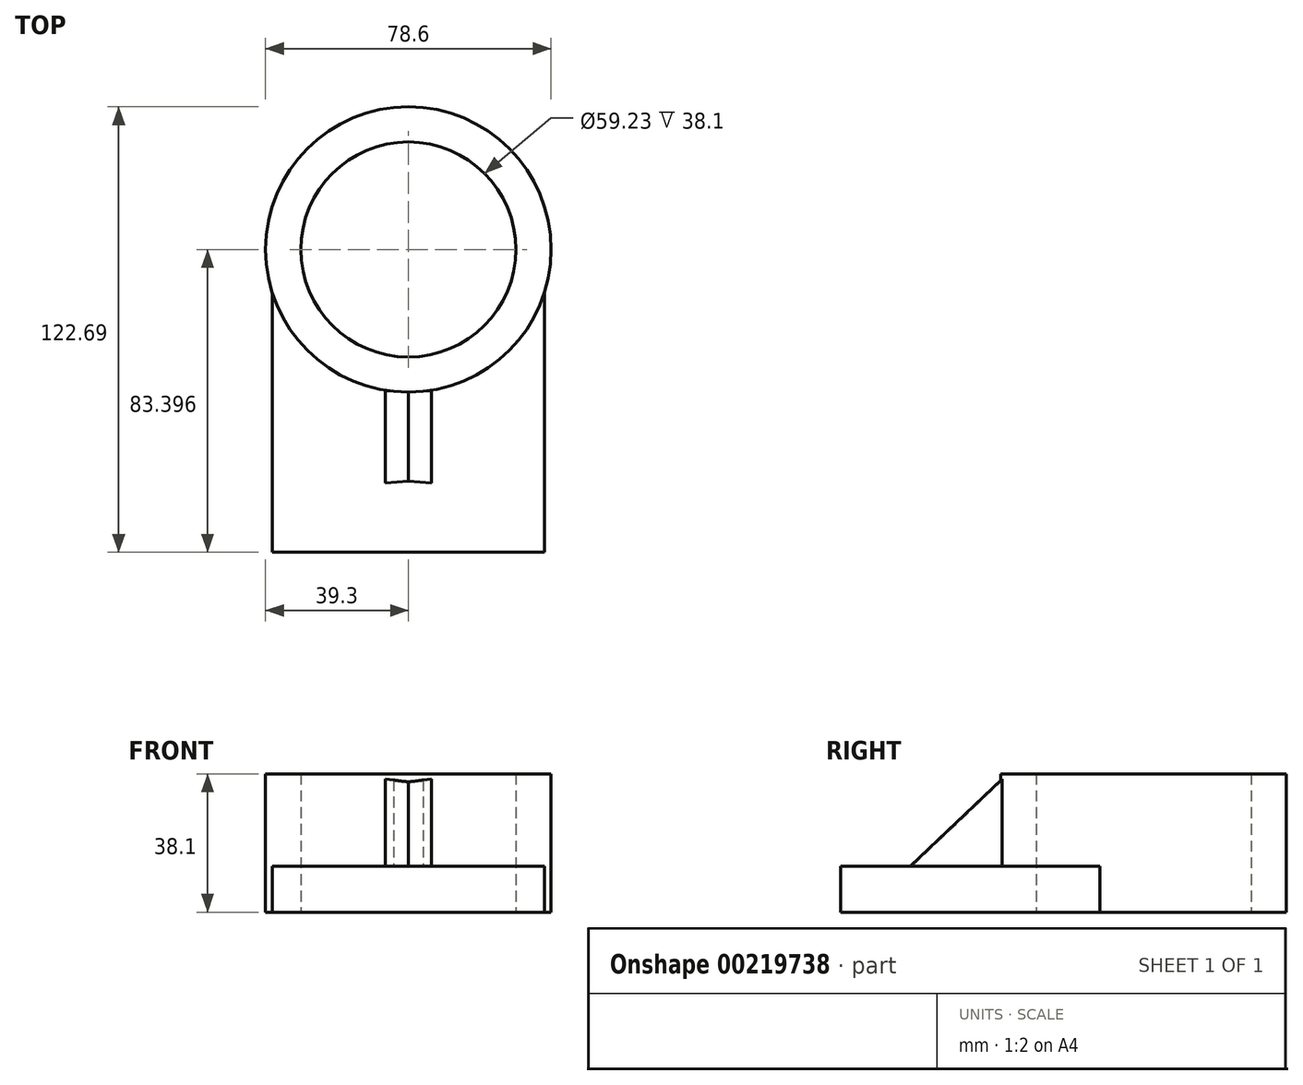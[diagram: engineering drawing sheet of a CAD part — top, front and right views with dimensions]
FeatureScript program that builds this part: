
annotation { "Feature Type Name" : "Feature", "Feature Type Description" : "" }
export const myFeature = defineFeature(function(context is Context, id is Id, definition is map)
    precondition{}
    {
        {
            var Q0;
            Q0=qCreatedBy(makeId("Top.planeOp"),FACE);
            var sketch = newSketch(context, id + "F0", { "sketchPlane" : qUnion([Q0])});
            skLineSegment(sketch, "E0.bottom", {"start": v(37.4, -35.68) * mm, "end": v(-37.4, -35.68) * mm});
            skLineSegment(sketch, "E0.top", {"start": v(37.4, 35.68) * mm, "end": v(-37.4, 35.68) * mm});
            skLineSegment(sketch, "E0.left", {"start": v(37.4, -35.68) * mm, "end": v(37.4, 35.68) * mm});
            skLineSegment(sketch, "E0.right", {"start": v(-37.4, -35.68) * mm, "end": v(-37.4, 35.68) * mm});
            skPoint(sketch, "E0.middle", {"position": v(0, 0) * mm});
            skSolve(sketch);
        }
        {
            var Q0;
            Q0=makeQuery(id+"F0.imprint","IMPRINT",FACE,{"disambiguationData":[TD([[makeQuery(id+"F0.imprint","IMPRINT",EDGE,{"derivedFrom":sQuery(id+"F0.wireOp",EDGE,"E0.bottom")}),-1.0]])]});
            extrude(context, id + "F1", {"entities" : qUnion([Q0]), "depth" : 12.7 * mm});
        }
        {
            var Q0;
            Q0=makeQuery(id+"F1.opExtrude","CAP_FACE",FACE,{"disambiguationData":[OSD([sQuery(id+"F0.wireOp",EDGE,"E0.bottom"),sQuery(id+"F0.wireOp",EDGE,"E0.top"),sQuery(id+"F0.wireOp",EDGE,"E0.left"),sQuery(id+"F0.wireOp",EDGE,"E0.right")])],"isStart":true});
            var sketch = newSketch(context, id + "F2", { "sketchPlane" : qUnion([Q0])});
            skCircle(sketch, "E1", {"center": v(0, -47.72) * mm, "radius": 39.3 * mm});
            skPoint(sketch, "E1.centerSnap0", {"position": v(0, -35.68) * mm});
            skCircle(sketch, "E2", {"center": v(0, -47.72) * mm, "radius": 29.61 * mm});
            skSolve(sketch);
        }
        {
            var Q0;
            {var subQ1=makeQuery(id+"F1.opExtrude","CAP_EDGE",EDGE,{"disambiguationData":[OSD([sQuery(id+"F0.wireOp",EDGE,"E0.top")])],"isStart":true});var subQ4=sQuery(id+"F2.wireOp",EDGE,"E2");var subQ5=makeQuery(id+"F2.imprint","INTERSECT",VERTEX,{"disambiguationData":[OD(0.0)],"derivedFrom":[subQ1,subQ4]});Q0=makeQuery(id+"F2.imprint","IMPRINT",FACE,{"disambiguationData":[TD([[makeQuery(id+"F2.imprint","IMPRINT",EDGE,{"disambiguationData":[TD([[subQ5,-1.0]])],"derivedFrom":subQ4}),-1.0]])]});}
            var Q1;
            {var subQ1=makeQuery(id+"F1.opExtrude","CAP_EDGE",EDGE,{"disambiguationData":[OSD([sQuery(id+"F0.wireOp",EDGE,"E0.top")])],"isStart":true});var subQ4=sQuery(id+"F2.wireOp",EDGE,"E2");var subQ5=makeQuery(id+"F2.imprint","INTERSECT",VERTEX,{"disambiguationData":[OD(0.0)],"derivedFrom":[subQ1,subQ4]});Q1=makeQuery(id+"F2.imprint","IMPRINT",FACE,{"disambiguationData":[TD([[makeQuery(id+"F2.imprint","IMPRINT",EDGE,{"disambiguationData":[TD([[subQ5,1.0]])],"derivedFrom":subQ4}),-1.0]])]});}
            extrude(context, id + "F3", {"entities" : qUnion([Q0, Q1]), "operationType" : NewBodyOperationType.ADD, "oppositeDirection" : true, "depth" : 38.1 * mm});
        }
        {
            var Q0;
            {var subQ0=sQuery(id+"F0.wireOp",EDGE,"E0.top");Q0=makeQuery(id+"F3.boolean.opBoolean","SPLIT",FACE,{"disambiguationData":[TD([makeQuery(id+"F1.opExtrude","SWEPT_FACE",FACE,{"disambiguationData":[OSD([subQ0])]})])],"derivedFrom":makeQuery(id+"F1.opExtrude","CAP_FACE",FACE,{"disambiguationData":[OSD([sQuery(id+"F0.wireOp",EDGE,"E0.bottom"),subQ0,sQuery(id+"F0.wireOp",EDGE,"E0.left"),sQuery(id+"F0.wireOp",EDGE,"E0.right")])],"isStart":false})});}
            extrude(context, id + "F4", {"entities" : qUnion([Q0]), "operationType" : NewBodyOperationType.REMOVE, "endBound" : BoundingType.SYMMETRIC, "oppositeDirection" : true, "depth" : 76.2 * mm});
        }
        {
            var Q0;
            Q0=qCreatedBy(makeId("Right.planeOp"),FACE);
            var sketch = newSketch(context, id + "F5", { "sketchPlane" : qUnion([Q0])});
            skLineSegment(sketch, "E3", {"start": v(8.42, 12.7) * mm, "end": v(8.42, 38.1) * mm});
            skLineSegment(sketch, "E4.0", {"start": v(-35.68, 12.7) * mm, "end": v(35.68, 12.7) * mm});
            skLineSegment(sketch, "E5", {"start": v(8.42, 35.9) * mm, "end": v(-16.07, 12.7) * mm});
            skLineSegment(sketch, "E6", {"start": v(-16.07, 12.7) * mm, "end": v(8.42, 12.7) * mm});
            skSolve(sketch);
        }
        {
            var Q0;
            Q0 = qSketchRegion(id + "F5", true);
            extrude(context, id + "F6", {"entities" : qUnion([Q0]), "operationType" : NewBodyOperationType.ADD, "endBound" : BoundingType.SYMMETRIC, "depth" : 12.7 * mm, "hasDraft" : true, "draftAngle" : 3 * degree});
        }
    });
